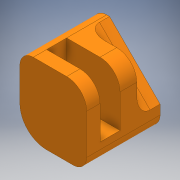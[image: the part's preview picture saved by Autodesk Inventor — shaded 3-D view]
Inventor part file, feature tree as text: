
AUTODESK INVENTOR PART (.ipt)
format: ipt  version: 2017 (Build 210142000, 142)  size: 261,632 bytes
history: native  units: mm
features: extrude x11, sketch x11, fillet x3, projected_geometry x1
ambient origin geometry x8: Origin, YZ Plane, XZ Plane, XY Plane, X Axis, Y Axis, Z Axis, Center Point
bodies: Solid1 (feature_tree)
feature tree (26):
  extrude  "Extrusion1"  Depth=3.0mm
  extrude  "Extrusion2"  Depth=3.0mm
  extrude  "Extrusion3"  Depth=0.5mm TaperAngle=0.0deg
  fillet  "Fillet1"  Radius=2.0mm
  sketch  "Sketch5"  dims[d10=2.0mm d11=2.0mm]
  sketch  "Sketch7"  dims[d12=3.3333mm d15=5.8mm]
  extrude  "Extrusion8"  Depth=2.0mm
  extrude  "Extrusion10"  Depth=5.8mm
  extrude  "Extrusion11"  Depth=1.3mm TaperAngle=0.0deg
  extrude  "Extrusion12"  Depth=1.0mm TaperAngle=0.0deg
  fillet  "Fillet3"  Radius=0.25mm
  extrude  "Extrusion14"  Depth=0.3mm TaperAngle=0.0deg
  extrude  "Extrusion15"  Depth=2.0mm
  extrude  "Extrusion16"  Depth=4.5mm TaperAngle=0.0deg
  fillet  "Fillet5"  [1 undecoded]
  extrude  "Extrusion17"  [1 undecoded]
  sketch  "Sketch1"  dims[d0=5.0mm d1=3.0mm]
  sketch  "Sketch2"  dims[d2=4.0mm d3=3.0mm]
  sketch  "Sketch3"  dims[d4=5.5mm d5=0.0mm d6=0.5mm d7=0.0mm d8=2.0mm d9=0.0mm]
  sketch  "Sketch11"  dims[d25=5.5mm d26=0.0mm d30=1.3mm d31=0.0mm]
  sketch  "Sketch12"  dims[d32=1.0mm d33=0.0mm d34=1.0mm d35=0.0mm d36=0.25mm]
  sketch  "Sketch14"  dims[d41=0.3mm d42=0.0mm d43=0.2mm d44=0.0mm]
  sketch  "Sketch15"  dims[d45=0.2mm d46=0.0mm d47=2.0mm]
  sketch  "Sketch16"  dims[d48=2.0mm d49=0.0mm d50=4.5mm d51=0.0mm]
  sketch  "Sketch17"
  projected_geometry  "Projected Loop2"
note: 2 required parameter values undecoded (feature->parameter linkage not recoverable at this tier; creation-order binding heuristic only, values carry confidence <= 0.55)
